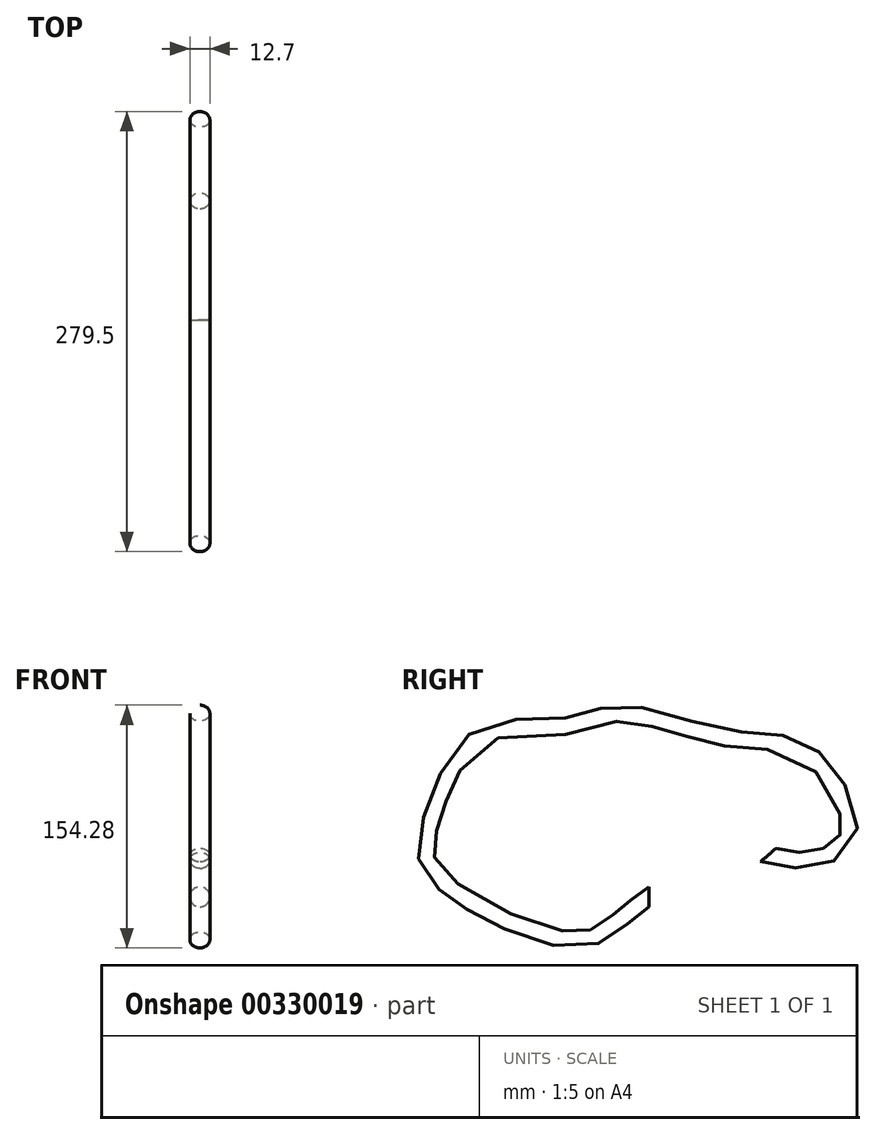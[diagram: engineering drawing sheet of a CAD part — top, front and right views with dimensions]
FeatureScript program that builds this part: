
annotation { "Feature Type Name" : "Feature", "Feature Type Description" : "" }
export const myFeature = defineFeature(function(context is Context, id is Id, definition is map)
    precondition{}
    {
        {
            var Q0;
            Q0=qCreatedBy(makeId("Right.planeOp"),FACE);
            var sketch = newSketch(context, id + "F0", { "sketchPlane" : qUnion([Q0])});
            skPoint(sketch, "E0.0.internal.orphan", {"position": v(0, -54.23) * mm});
            skPoint(sketch, "E1.2.internal.orphan", {"position": v(-22, -54.23) * mm});
            skFitSpline(sketch, "E2", {"points": [v(0, 0) * mm, v(-15.72, -12.2) * mm, v(-42.08, -26.9) * mm, v(-95.92, -12.58) * mm, v(-123.4, 3.6) * mm, v(-140.73, 23.56) * mm, v(-133.2, 63.1) * mm, v(-104.58, 103) * mm, v(-49.23, 109.03) * mm, v(-17.23, 116.56) * mm, v(46.4, 101.5) * mm, v(89.33, 96.23) * mm, v(115.68, 75.52) * mm, v(126.23, 39) * mm, v(104.01, 23.94) * mm, v(75.77, 26.58) * mm], "startDerivative": vector(-311.48, -230.55) * mm, "endDerivative": vector(-479.82, 108.82) * mm});
            skSolve(sketch);
        }
        {
            var Q0;
            Q0=qCreatedBy(makeId("Front.planeOp"),FACE);
            var sketch = newSketch(context, id + "F1", { "sketchPlane" : qUnion([Q0])});
            skCircle(sketch, "E3", {"center": v(0, 0) * mm, "radius": 6.35 * mm});
            skSolve(sketch);
        }
        {
            var Q0;
            Q0=makeQuery(id+"F1.imprint","IMPRINT",FACE,{"disambiguationData":[TD([[makeQuery(id+"F1.imprint","IMPRINT",EDGE,{"derivedFrom":sQuery(id+"F1.wireOp",EDGE,"E3")}),1.0]])]});
            var Q1;
            Q1=sQuery(id+"F0.wireOp",EDGE,"E2");
            sweep(context, id + "F2", {"profiles" : qUnion([Q0]), "path" : qUnion([Q1])});
        }
    });
